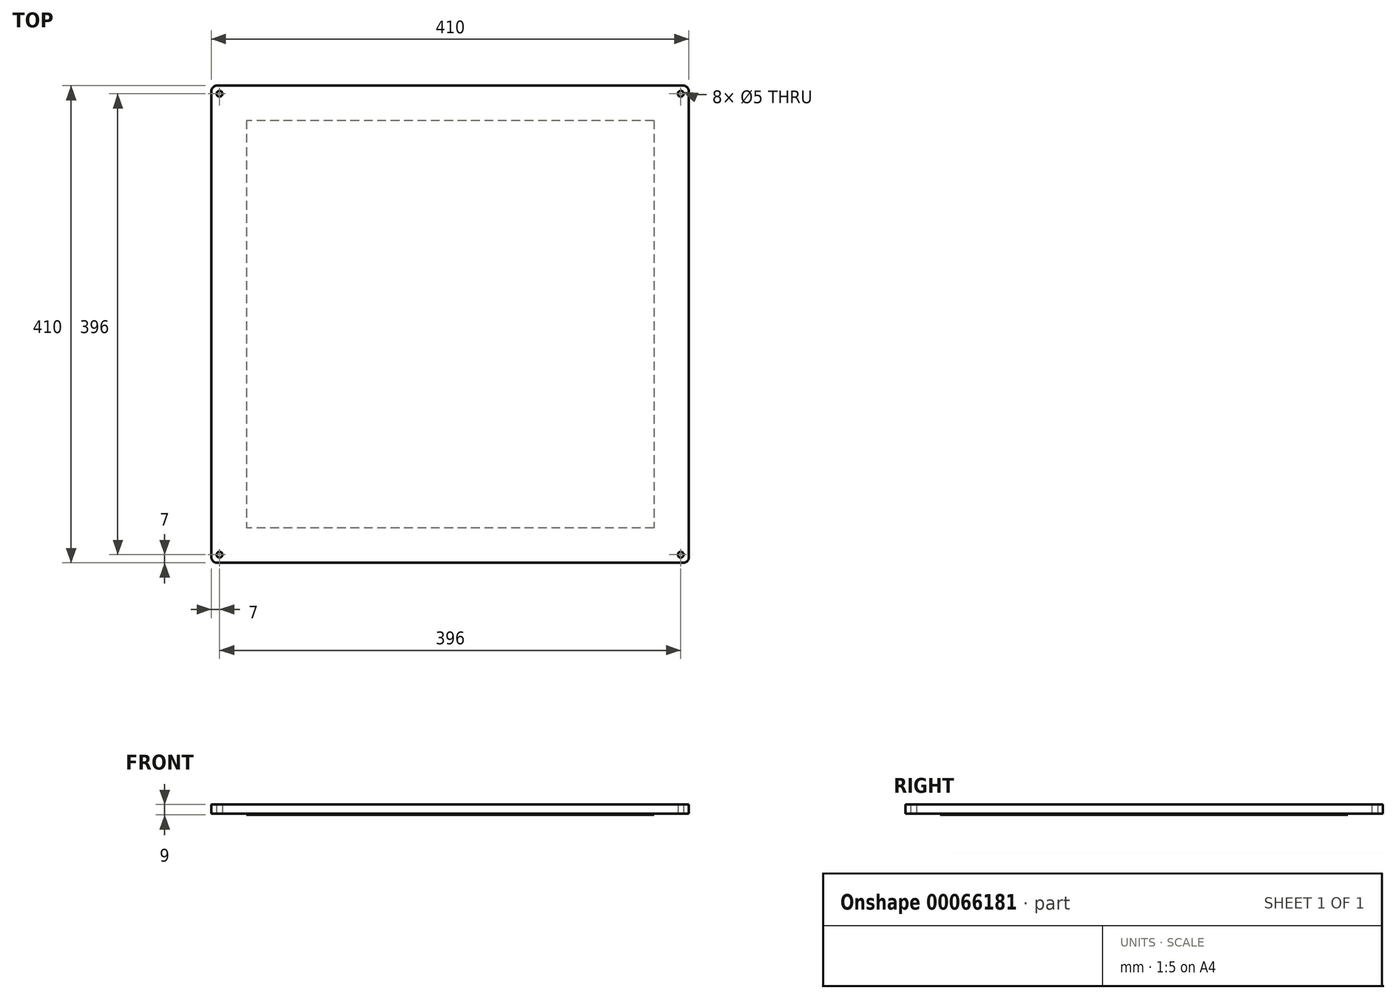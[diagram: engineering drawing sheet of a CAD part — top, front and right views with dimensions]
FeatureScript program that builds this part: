
annotation { "Feature Type Name" : "Feature", "Feature Type Description" : "" }
export const myFeature = defineFeature(function(context is Context, id is Id, definition is map)
    precondition{}
    {
        {
            var Q0;
            Q0=qCreatedBy(makeId("Top.planeOp"),FACE);
            var sketch = newSketch(context, id + "F0", { "sketchPlane" : qUnion([Q0])});
            skLineSegment(sketch, "E0.bottom", {"start": v(205, 205) * mm, "end": v(-205, 205) * mm});
            skLineSegment(sketch, "E0.top", {"start": v(205, -205) * mm, "end": v(-205, -205) * mm});
            skLineSegment(sketch, "E0.left", {"start": v(205, 205) * mm, "end": v(205, -205) * mm});
            skLineSegment(sketch, "E0.right", {"start": v(-205, 205) * mm, "end": v(-205, -205) * mm});
            skPoint(sketch, "E0.middle", {"position": v(0, 0) * mm});
            skLineSegment(sketch, "E1.bottom", {"start": v(198, 198) * mm, "end": v(-198, 198) * mm, "construction": true});
            skLineSegment(sketch, "E1.top", {"start": v(198, -198) * mm, "end": v(-198, -198) * mm, "construction": true});
            skLineSegment(sketch, "E1.left", {"start": v(198, 198) * mm, "end": v(198, -198) * mm, "construction": true});
            skLineSegment(sketch, "E1.right", {"start": v(-198, 198) * mm, "end": v(-198, -198) * mm, "construction": true});
            skCircle(sketch, "E2", {"center": v(-198, 198) * mm, "radius": 2.5 * mm});
            skCircle(sketch, "E3", {"center": v(198, 198) * mm, "radius": 2.5 * mm});
            skCircle(sketch, "E4", {"center": v(-198, -198) * mm, "radius": 2.5 * mm});
            skCircle(sketch, "E5", {"center": v(198, -198) * mm, "radius": 2.5 * mm});
            skSolve(sketch);
        }
        {
            var Q0;
            Q0=makeQuery(id+"F0.imprint","IMPRINT",FACE,{"disambiguationData":[TD([[makeQuery(id+"F0.imprint","IMPRINT",EDGE,{"derivedFrom":sQuery(id+"F0.wireOp",EDGE,"E0.bottom")}),1.0]])]});
            extrude(context, id + "F1", {"entities" : qUnion([Q0]), "depth" : 8 * mm, "offsetDistance" : 25 * mm});
        }
        {
            var Q0;
            Q0=makeQuery(id+"F1.opExtrude","SWEPT_EDGE",EDGE,{"disambiguationData":[OSD([sQuery(id+"F0.wireOp",EDGE,"E0.top"),sQuery(id+"F0.wireOp",EDGE,"E0.right")])]});
            var Q1;
            Q1=makeQuery(id+"F1.opExtrude","SWEPT_EDGE",EDGE,{"disambiguationData":[OSD([sQuery(id+"F0.wireOp",EDGE,"E0.top"),sQuery(id+"F0.wireOp",EDGE,"E0.left")])]});
            var Q2;
            Q2=makeQuery(id+"F1.opExtrude","SWEPT_EDGE",EDGE,{"disambiguationData":[OSD([sQuery(id+"F0.wireOp",EDGE,"E0.bottom"),sQuery(id+"F0.wireOp",EDGE,"E0.left")])]});
            var Q3;
            Q3=makeQuery(id+"F1.opExtrude","SWEPT_EDGE",EDGE,{"disambiguationData":[OSD([sQuery(id+"F0.wireOp",EDGE,"E0.bottom"),sQuery(id+"F0.wireOp",EDGE,"E0.right")])]});
            fillet(context, id + "F2", {"entities" : qUnion([Q0, Q1, Q2, Q3]), "radius" : 5 * mm, "tangentPropagation" : true, "allowEdgeOverflow" : false});
        }
        {
            var Q0;
            Q0=makeQuery(id+"F1.opExtrude","CAP_FACE",FACE,{"disambiguationData":[OSD([sQuery(id+"F0.wireOp",EDGE,"E0.bottom"),sQuery(id+"F0.wireOp",EDGE,"E0.top"),sQuery(id+"F0.wireOp",EDGE,"E0.left"),sQuery(id+"F0.wireOp",EDGE,"E0.right"),sQuery(id+"F0.wireOp",EDGE,"E2"),sQuery(id+"F0.wireOp",EDGE,"E3"),sQuery(id+"F0.wireOp",EDGE,"E4"),sQuery(id+"F0.wireOp",EDGE,"E5")])],"isStart":true});
            var sketch = newSketch(context, id + "F3", { "sketchPlane" : qUnion([Q0])});
            skLineSegment(sketch, "E6.bottom", {"start": v(175, -175) * mm, "end": v(-175, -175) * mm});
            skLineSegment(sketch, "E6.top", {"start": v(175, 175) * mm, "end": v(-175, 175) * mm});
            skLineSegment(sketch, "E6.left", {"start": v(175, -175) * mm, "end": v(175, 175) * mm});
            skLineSegment(sketch, "E6.right", {"start": v(-175, -175) * mm, "end": v(-175, 175) * mm});
            skPoint(sketch, "E6.middle", {"position": v(0, 0) * mm});
            skLineSegment(sketch, "E7", {"start": v(-198, 198) * mm, "end": v(198, -198) * mm, "construction": true});
            skSolve(sketch);
        }
        {
            var Q0;
            Q0=makeQuery(id+"F3.imprint","IMPRINT",FACE,{"disambiguationData":[TD([[makeQuery(id+"F3.imprint","IMPRINT",EDGE,{"derivedFrom":sQuery(id+"F3.wireOp",EDGE,"E6.bottom")}),-1.0]])]});
            extrude(context, id + "F4", {"entities" : qUnion([Q0]), "depth" : 1 * mm, "offsetDistance" : 25 * mm});
        }
    });
